# Revit family: BuroSeating_Konfurb Block
name_source: partatom
category: Furniture
units: mm (PartAtom-declared; Revit-internal decimal feet)

## family parameters
Always vertical = Yes
Cut with Voids When Loaded = No
OmniClass Number = 23.40.70.14.64.11
OmniClass Title = Office Furniture
Room Calculation Point = No
Shared = Yes
Work Plane-Based = No

## types (5) — shared parameters
Assembly Code = E2020
BaseOffset = 18 mm  [stored 0.0590551 ft]
FeetDiameter = 50 mm  [stored 0.164042 ft]
FeetInset = 50 mm  [stored 0.164042 ft]
FeetMaterial = BuroSeating_Plastic_Black
Manufacturer = Buro Seating
Model = KON740A
ProductGroup = Konfurb Halo
ProductPageURL AU = https://buroseating.com
ProductPageURL NZ = https://buroseating.co.nz
ProductRange = Konfurb
URL = https://buroseating.co.nz
URL AU = https://buroseating.com
WarrantyDescription = Full 5 year guarantee (excluding upholstery)

## per-type parameters (varying)
| type | Default Elevation | Description | NominalDepth | NominalHeight | NominalLength |
| B1 | 0 mm  [stored 0 ft] | Konfurb Block Single Low Back | 250 mm  [stored 0.82021 ft] | 700 mm  [stored 2.29659 ft] | 800 mm  [stored 2.62467 ft] |
| B2 | 18 mm  [stored 0.0590551 ft] | Konfurb Block Double Low Back | 250 mm  [stored 0.82021 ft] | 700 mm  [stored 2.29659 ft] | 1600 mm  [stored 5.24934 ft] |
| B3 | 0 mm  [stored 0 ft] | Konfurb Block Single HIgh Back | 250 mm  [stored 0.82021 ft] | 1050 mm | 800 mm  [stored 2.62467 ft] |
| S1 | 0 mm  [stored 0 ft] | Konfurb Block Single Seat | 560 mm  [stored 1.83727 ft] | 410 mm  [stored 1.34514 ft] | 800 mm  [stored 2.62467 ft] |
| S2 | 0 mm  [stored 0 ft] | Konfurb Block Double Seat | 560 mm  [stored 1.83727 ft] | 410 mm  [stored 1.34514 ft] | 1600 mm  [stored 5.24934 ft] |

note: [stored X ft] marks values corroborated as IEEE doubles in the binary element streams (Revit-internal decimal feet)

## geometry (parser evidence)
native form markers: Sweep x5
no freeform markers — native parametric forms only
